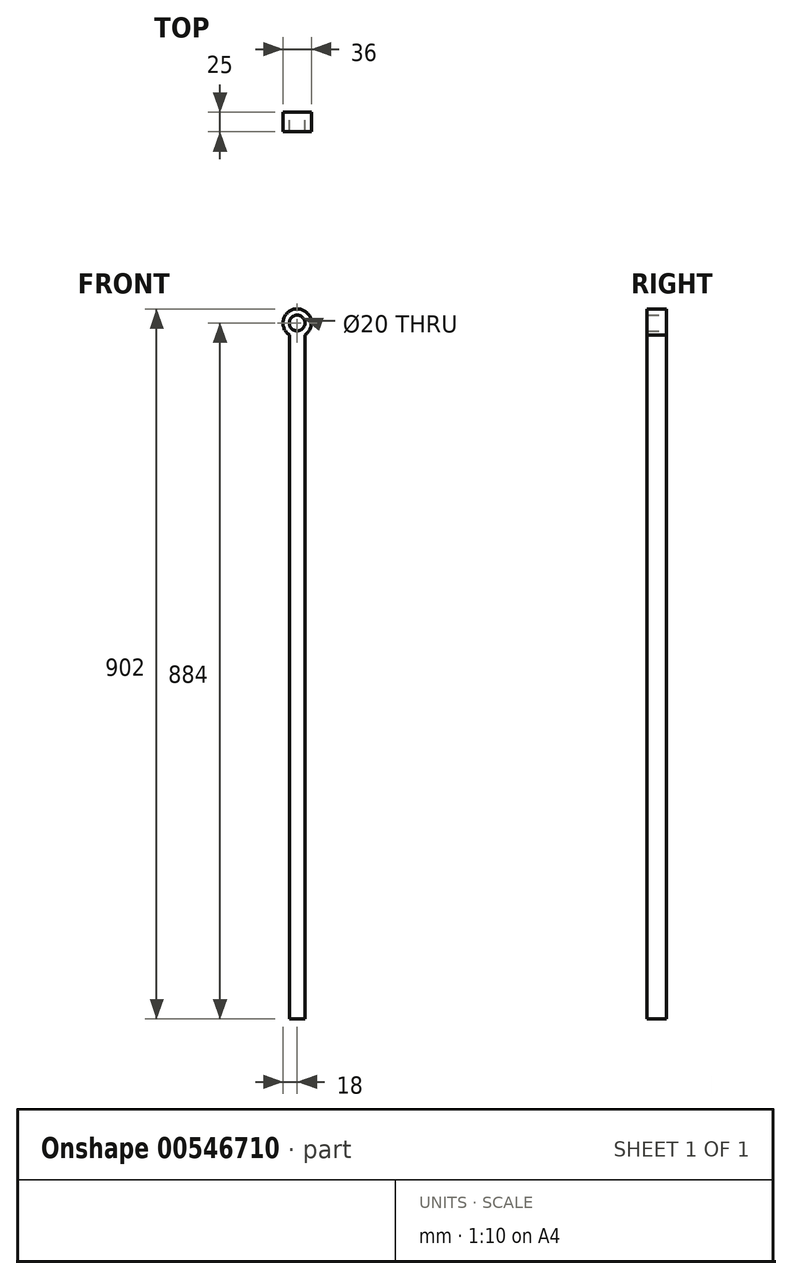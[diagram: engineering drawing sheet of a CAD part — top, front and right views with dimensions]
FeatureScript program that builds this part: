
annotation { "Feature Type Name" : "Feature", "Feature Type Description" : "" }
export const myFeature = defineFeature(function(context is Context, id is Id, definition is map)
    precondition{}
    {
        {
            var Q0;
            Q0=qCreatedBy(makeId("Front.planeOp"),FACE);
            var sketch = newSketch(context, id + "F0", { "sketchPlane" : qUnion([Q0])});
            skCircle(sketch, "E0", {"center": v(0, 0) * mm, "radius": 10 * mm});
            skArc(sketch, "E1", {"start": v(10, -14.97) * mm, "mid": v(0, 18) * mm, "end": v(-10, -14.97) * mm});
            skLineSegment(sketch, "E2.top", {"start": v(-10, -884) * mm, "end": v(10, -884) * mm});
            skLineSegment(sketch, "E2.left", {"start": v(-10, -14.97) * mm, "end": v(-10, -884) * mm});
            skLineSegment(sketch, "E2.right", {"start": v(10, -14.97) * mm, "end": v(10, -884) * mm});
            skSolve(sketch);
        }
        {
            var Q0;
            Q0=makeQuery(id+"F0.imprint","IMPRINT",FACE,{"disambiguationData":[TD([[makeQuery(id+"F0.imprint","IMPRINT",EDGE,{"derivedFrom":sQuery(id+"F0.wireOp",EDGE,"E0")}),-1.0]])]});
            extrude(context, id + "F1", {"entities" : qUnion([Q0]), "depth" : 25 * mm, "offsetDistance" : 25 * mm});
        }
    });
